# Revit family: CENTUM Spannschuh L, XL200
name_source: partatom
category: HLS-Bauteile
units: mm (PartAtom-declared; Revit-internal decimal feet)

## family parameters
Arbeitsebenenbasiert = Ja
Beim Laden mit Abzugskörper schneiden = Nein
Bemaßung runder Anschluss = Durchmesser verwenden
Beschriftungsausrichtung beibehalten = Nein
Gemeinsam genutzt = Ja
Immer vertikal = Nein
Raumberechnungspunkt = Nein
Teiletyp = Normal

## types (1)
- Centum Spannschuh L XL200
    Artikelnummer = 1662004010
    EAN = 4250928449931
    Fabrikat = MEFA
    Firma = MEFA Befestigungs- und Montagesysteme GmbH
    Gewicht = 7.22 kg
    Gewicht pro Bauteil = 7.22 kg
    Kurztext1 = Spannschuh CENTUM L
    Kurztext2 = für Profiltyp XL 200
    Material = Stahl
    Materialname = S235
    Mengeneinheit = Set
    Oberflaeche = feuerstückverzinkt
    Profiltyp = XL 200
    Sicherheitsfaktor = 1.54
    Vorgabe-Ansicht = 1219 mm
    max Klemmdicke = 20 mm  [stored 0.0656168 ft]
    max. Stegdicke Träger = 20 mm
    max. zul. Last Fx = 20.00 kN
    max. zul. Last Fy = 4.20 kN
    max. zul. Last Fz = 22.50 kN
    max. zul. Querlast = 0.00 kN-m
    min. Klemmdicke = 13 mm
    vpe = 1

note: [stored X ft] marks values corroborated as IEEE doubles in the binary element streams (Revit-internal decimal feet)

## geometry (parser evidence)
native form markers: Sweep x4
no freeform markers — native parametric forms only
